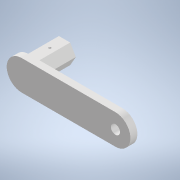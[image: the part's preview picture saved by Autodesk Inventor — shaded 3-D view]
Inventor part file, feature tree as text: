
AUTODESK INVENTOR PART (.ipt)
format: ipt  version: 2022 (Build 260153000, 153)  size: 156,160 bytes
history: native  units: mm
features: reference x13, other x5, extrude x4, sketch x4, fillet x1, projected_geometry x1
ambient origin geometry x8: Origin, YZ Plane, XZ Plane, XY Plane, X Axis, Y Axis, Z Axis, Center Point
bodies: Solid1 (feature_tree)
feature tree (28):
  extrude  "Extrusion1"  Depth=3.0mm TaperAngle=0.0deg
  extrude  "Extrusion2"  Depth=1.0mm
  sketch  "Sketch3"  dims[d11=10.0mm d12=0.0mm d13=15.0mm]
  fillet  "Fillet1"  Radius=1.25mm
  extrude  "Extrusion4"  Depth=15.0mm
  extrude  "Extrusion5"  Depth=3.5mm TaperAngle=0.0deg
  sketch  "Sketch1"  dims[d0=15.0mm d1=0.0mm d2=3.0mm d3=0.0mm]
  reference  "Reference1"
  reference  "Reference2"
  reference  "Reference3"
  reference  "Reference4"
  reference  "Reference5"
  reference  "Reference6"
  reference  "Reference7"
  reference  "Reference8"
  reference  "Reference9"
  reference  "Reference10"
  reference  "Reference11"
  reference  "Reference12"
  sketch  "Sketch2"  dims[d5=4.6mm d9=1.0mm d10=1.25mm]
  sketch  "Sketch4"  dims[d14=47.0mm d15=3.5mm d16=0.0mm]
  projected_geometry  "Projected Loop1"
  reference  "Reference13"
  other  "Caja_Reductora.iam"
  other  "Hombro_Ejes:12"
  other  "Rodamiento_Ejes:8"
  other  "Assembly_Final.iam"
  other  "Caja_Reductora:1"
